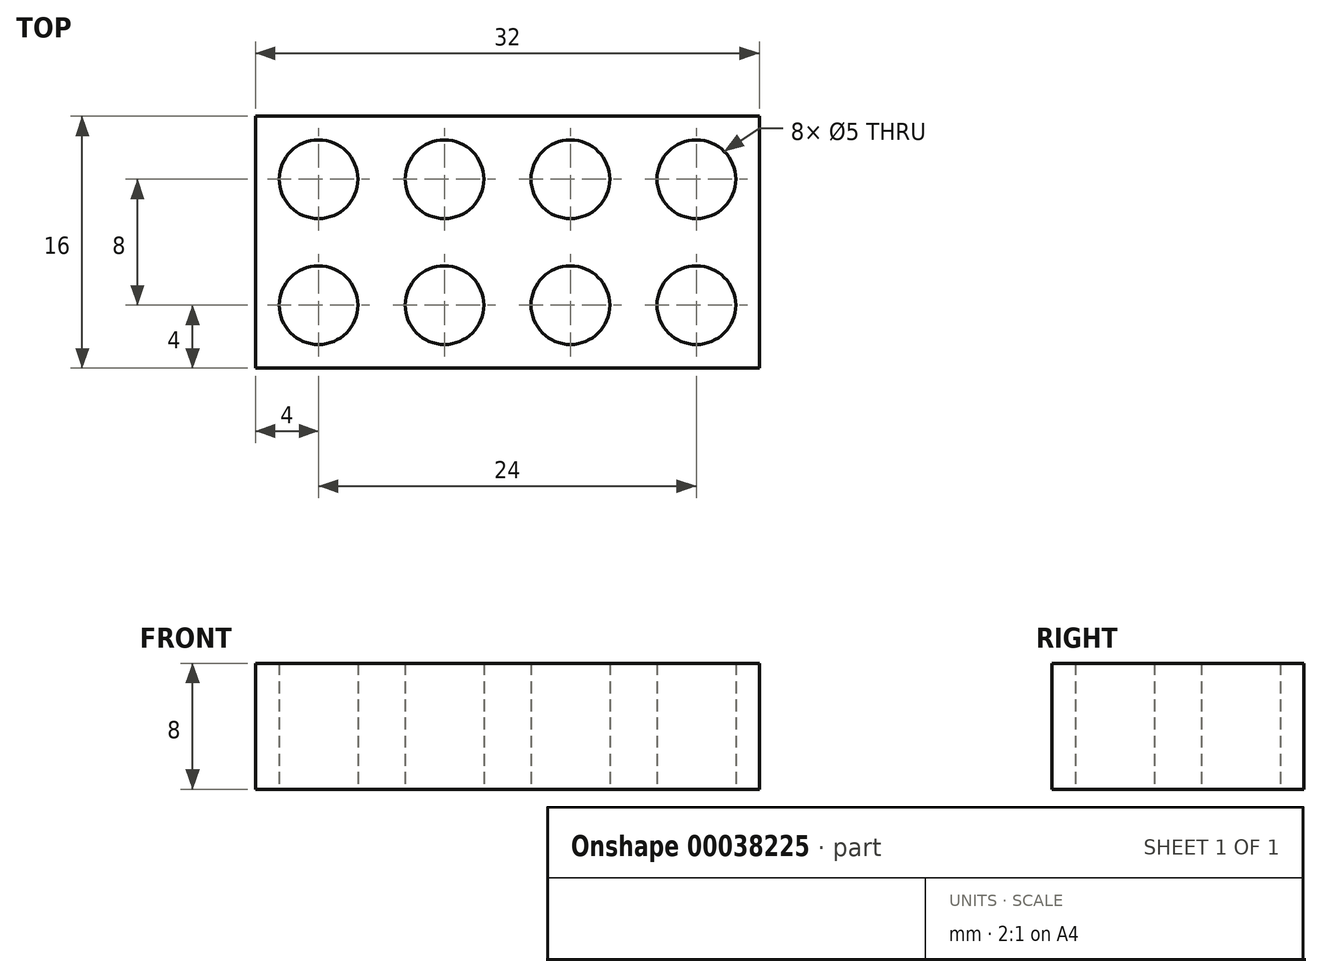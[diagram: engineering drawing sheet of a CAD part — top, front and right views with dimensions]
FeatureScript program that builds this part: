
annotation { "Feature Type Name" : "Feature", "Feature Type Description" : "" }
export const myFeature = defineFeature(function(context is Context, id is Id, definition is map)
    precondition{}
    {
        {
            var Q0;
            Q0=qCreatedBy(makeId("Top.planeOp"),FACE);
            var sketch = newSketch(context, id + "F0", { "sketchPlane" : qUnion([Q0])});
            skLineSegment(sketch, "E0.rect.bottom", {"start": v(16, 8) * mm, "end": v(-16, 8) * mm});
            skLineSegment(sketch, "E0.rect.top", {"start": v(16, -8) * mm, "end": v(-16, -8) * mm});
            skLineSegment(sketch, "E0.rect.left", {"start": v(16, 8) * mm, "end": v(16, -8) * mm});
            skLineSegment(sketch, "E0.rect.right", {"start": v(-16, 8) * mm, "end": v(-16, -8) * mm});
            skPoint(sketch, "E0.rect.middle", {"position": v(0, 0) * mm});
            skLineSegment(sketch, "E1", {"start": v(-16, 9.06) * mm, "end": v(-12, 9.06) * mm, "construction": true});
            skLineSegment(sketch, "E2", {"start": v(-12, 9.06) * mm, "end": v(-4, 9.06) * mm, "construction": true});
            skLineSegment(sketch, "E3", {"start": v(-4, 9.06) * mm, "end": v(4, 9.06) * mm, "construction": true});
            skLineSegment(sketch, "E4", {"start": v(4, 9.06) * mm, "end": v(12, 9.06) * mm, "construction": true});
            skLineSegment(sketch, "E5", {"start": v(12, 9.06) * mm, "end": v(16, 9.06) * mm, "construction": true});
            skLineSegment(sketch, "E6", {"start": v(16, 9.06) * mm, "end": v(16.12, 9.46) * mm, "construction": true});
            skLineSegment(sketch, "E7", {"start": v(-17.68, 8) * mm, "end": v(-17.68, 4) * mm, "construction": true});
            skLineSegment(sketch, "E8", {"start": v(-17.68, 4) * mm, "end": v(-17.68, 0) * mm, "construction": true});
            skLineSegment(sketch, "E9", {"start": v(-17.68, 0) * mm, "end": v(-17.68, -4) * mm, "construction": true});
            skLineSegment(sketch, "E10", {"start": v(-17.68, -4) * mm, "end": v(-17.68, -8) * mm, "construction": true});
            skLineSegment(sketch, "E11", {"start": v(-12, 7.33) * mm, "end": v(-12, -8) * mm, "construction": true});
            skLineSegment(sketch, "E12", {"start": v(-4, 7.33) * mm, "end": v(-4, -8) * mm, "construction": true});
            skLineSegment(sketch, "E13", {"start": v(4, 8) * mm, "end": v(4, -8) * mm, "construction": true});
            skLineSegment(sketch, "E14", {"start": v(12, 8) * mm, "end": v(12, -8) * mm, "construction": true});
            skLineSegment(sketch, "E15", {"start": v(-16, 4) * mm, "end": v(16, 4) * mm, "construction": true});
            skLineSegment(sketch, "E16", {"start": v(-16, 0) * mm, "end": v(16, 0) * mm, "construction": true});
            skLineSegment(sketch, "E17", {"start": v(-16, -4) * mm, "end": v(16, -4) * mm, "construction": true});
            skCircle(sketch, "E18", {"center": v(-12, 4) * mm, "radius": 2.5 * mm});
            skCircle(sketch, "E19", {"center": v(-12, -4) * mm, "radius": 2.5 * mm});
            skCircle(sketch, "E20", {"center": v(-4, 4) * mm, "radius": 2.5 * mm});
            skCircle(sketch, "E21", {"center": v(-4, -4) * mm, "radius": 2.5 * mm});
            skCircle(sketch, "E22.MirrorC", {"center": v(4, 4) * mm, "radius": 2.5 * mm});
            skCircle(sketch, "E23.MirrorC", {"center": v(12, 4) * mm, "radius": 2.5 * mm});
            skCircle(sketch, "E24.MirrorC", {"center": v(12, -4) * mm, "radius": 2.5 * mm});
            skCircle(sketch, "E25.MirrorC", {"center": v(4, -4) * mm, "radius": 2.5 * mm});
            skSolve(sketch);
        }
        {
            var Q0;
            Q0=makeQuery(id+"F0.imprint","IMPRINT",FACE,{"disambiguationData":[TD([[makeQuery(id+"F0.imprint","IMPRINT",EDGE,{"derivedFrom":sQuery(id+"F0.wireOp",EDGE,"E0.rect.bottom")}),1.0]])]});
            extrude(context, id + "F1", {"entities" : qUnion([Q0]), "depth" : 8 * mm});
        }
    });
